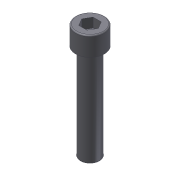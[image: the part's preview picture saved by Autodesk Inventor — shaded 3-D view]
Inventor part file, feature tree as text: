
AUTODESK INVENTOR PART (.ipt)
format: ipt  version: 2012 (Build 160160000, 160)  size: 104,960 bytes
history: native  units: in
note: dims shown in document units (in); Inventor stores cm internally (conversion verified against a paired STEP export)
features: extrude x3, sketch x3, fillet x1
ambient origin geometry x8: Origin, YZ Plane, XZ Plane, XY Plane, X Axis, Y Axis, Z Axis, Center Point
bodies: Solid1 (feature_tree)
feature tree (7):
  extrude  "Extrusion1"  Depth=1.25in TaperAngle=0.0deg
  extrude  "Extrusion2"  Depth=0.25in TaperAngle=0.0deg
  extrude  "Extrusion3"  Depth=0.125in TaperAngle=0.0deg
  fillet  "Fillet1"  Radius=0.0156in
  sketch  "Sketch1"  dims[d0=0.25in d1=1.25in d2=0.0in]
  sketch  "Sketch2"  dims[d3=0.375in d4=0.25in d5=0.0in]
  sketch  "Sketch3"  dims[d6=0.1875in d7=0.125in d8=0.0in d9=0.0156in]
